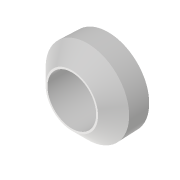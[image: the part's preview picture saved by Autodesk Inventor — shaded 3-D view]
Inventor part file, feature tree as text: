
AUTODESK INVENTOR PART (.ipt)
format: ipt  version: 2022 (Build 260153000, 153)  size: 100,864 bytes
history: native  units: mm
features: revolve x1, sketch x1
ambient origin geometry x8: Origin, YZ Plane, XZ Plane, XY Plane, X Axis, Y Axis, Z Axis, Center Point
bodies: Volumenkörper1 (feature_tree)
feature tree (2):
  revolve  "Umdrehung1"
  sketch  "Skizze1"  dims[d0=3.35mm d1=5.65mm d2=5.75mm d3=5.0mm d4=45.0deg d5=90.0deg]
